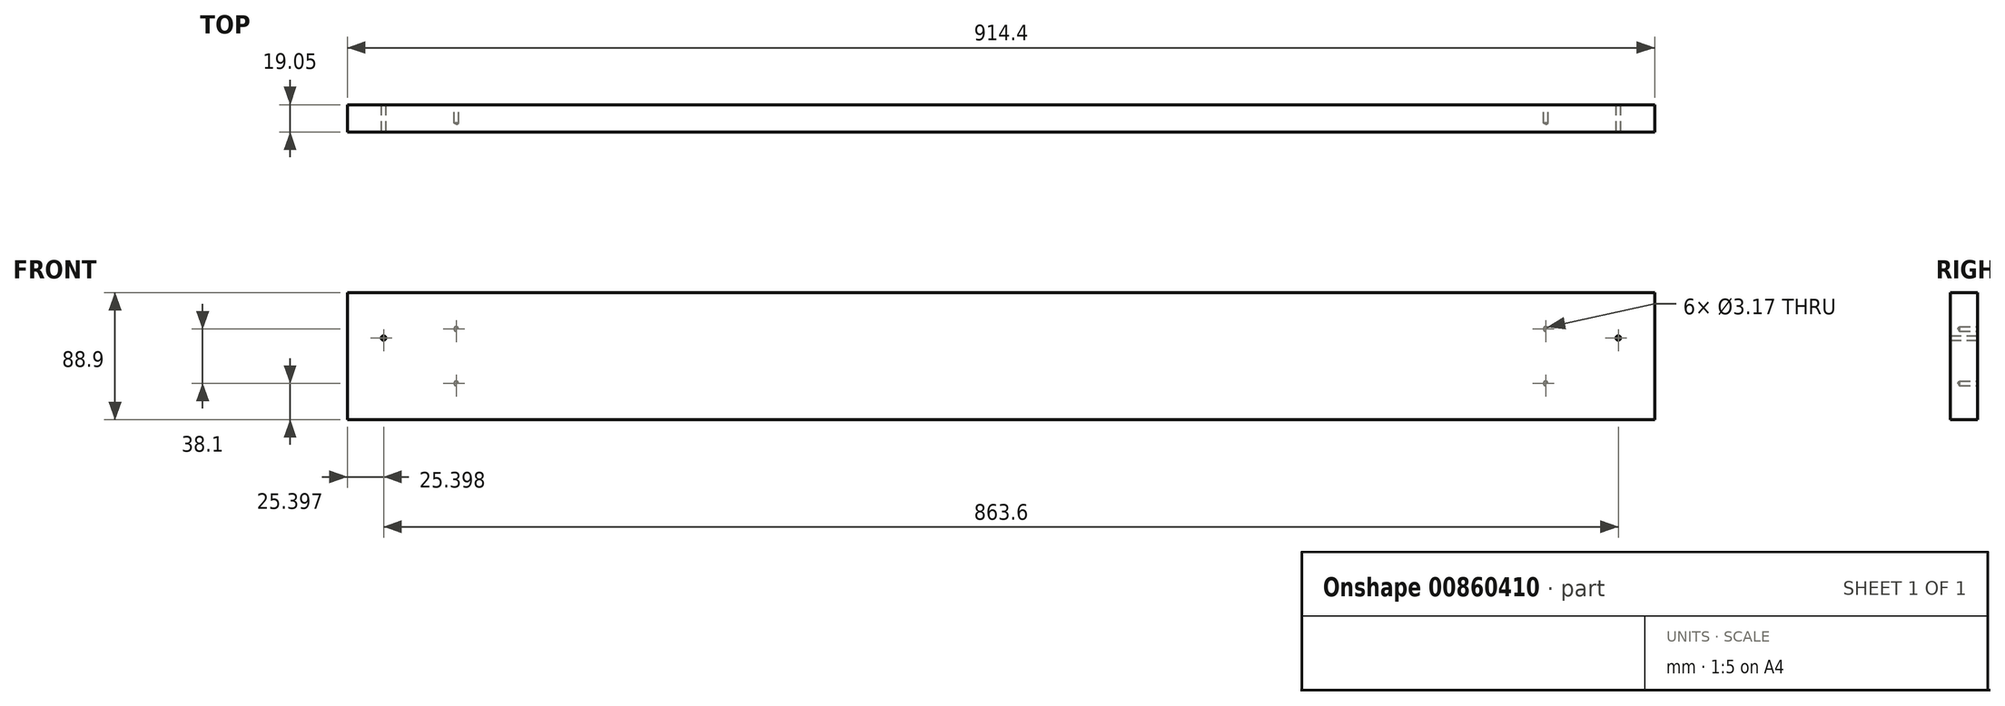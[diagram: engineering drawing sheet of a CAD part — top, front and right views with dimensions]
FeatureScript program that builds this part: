
annotation { "Feature Type Name" : "Feature", "Feature Type Description" : "" }
export const myFeature = defineFeature(function(context is Context, id is Id, definition is map)
    precondition{}
    {
        {
            var Q0;
            Q0=qCreatedBy(makeId("Front.planeOp"),FACE);
            var sketch = newSketch(context, id + "F0", { "sketchPlane" : qUnion([Q0])});
            skLineSegment(sketch, "E0.bottom", {"start": v(-572.65, 53.18) * mm, "end": v(341.75, 53.18) * mm});
            skLineSegment(sketch, "E0.top", {"start": v(-572.65, -35.72) * mm, "end": v(341.75, -35.72) * mm});
            skLineSegment(sketch, "E0.left", {"start": v(-572.65, 53.18) * mm, "end": v(-572.65, -35.72) * mm});
            skLineSegment(sketch, "E0.right", {"start": v(341.75, 53.18) * mm, "end": v(341.75, -35.72) * mm});
            skSolve(sketch);
        }
        {
            var Q0;
            Q0=makeQuery(id+"F0.imprint","IMPRINT",FACE,{"disambiguationData":[TD([[makeQuery(id+"F0.imprint","IMPRINT",EDGE,{"derivedFrom":sQuery(id+"F0.wireOp",EDGE,"E0.bottom")}),-1.0]])]});
            extrude(context, id + "F1", {"entities" : qUnion([Q0]), "depth" : 19.05 * mm, "offsetDistance" : 25.4 * mm});
        }
        {
            var Q0;
            Q0=makeQuery(id+"F1.opExtrude","CAP_FACE",FACE,{"disambiguationData":[OSD([sQuery(id+"F0.wireOp",EDGE,"E0.bottom"),sQuery(id+"F0.wireOp",EDGE,"E0.top"),sQuery(id+"F0.wireOp",EDGE,"E0.left"),sQuery(id+"F0.wireOp",EDGE,"E0.right")])],"isStart":true});
            var sketch = newSketch(context, id + "F2", { "sketchPlane" : qUnion([Q0])});
            skLineSegment(sketch, "E1", {"start": v(-265.55, -35.72) * mm, "end": v(-265.55, 53.18) * mm, "construction": true});
            skLineSegment(sketch, "E2", {"start": v(496.45, -35.72) * mm, "end": v(496.45, 53.18) * mm, "construction": true});
            skPoint(sketch, "E3", {"position": v(496.45, -10.32) * mm});
            skPoint(sketch, "E4", {"position": v(496.45, 27.78) * mm});
            skPoint(sketch, "E5", {"position": v(-265.55, -10.32) * mm});
            skPoint(sketch, "E6", {"position": v(-265.55, 27.78) * mm});
            skSolve(sketch);
        }
        {
            var Q0;
            Q0=sQuery(id+"F2.wireOp",VERTEX,"E5");
            var Q1;
            Q1=sQuery(id+"F2.wireOp",VERTEX,"E6");
            var Q2;
            Q2=sQuery(id+"F2.wireOp",VERTEX,"E3");
            var Q3;
            Q3=sQuery(id+"F2.wireOp",VERTEX,"E4");
            var Q4;
            Q4=makeQuery(id+"F1.opExtrude","SWEPT_BODY",BODY,{"disambiguationData":[OSD([sQuery(id+"F0.wireOp",EDGE,"E0.bottom"),sQuery(id+"F0.wireOp",EDGE,"E0.top"),sQuery(id+"F0.wireOp",EDGE,"E0.left"),sQuery(id+"F0.wireOp",EDGE,"E0.right")])]});
            hole(context, id + "F3", {"style" : HoleStyle.SIMPLE, "endStyle" : HoleEndStyle.BLIND, "holeDiameter" : 3.17 * mm, "majorDiameter" : 6.35 * mm, "holeDepth" : 12.7 * mm, "isTappedThrough" : true, "tappedDepth" : 12.7 * mm, "tapClearance" : 3, "locations" : qUnion([Q0, Q1, Q2, Q3]), "scope" : qUnion([Q4])});
        }
        {
            var Q0;
            Q0=makeQuery(id+"F1.opExtrude","CAP_FACE",FACE,{"disambiguationData":[OSD([sQuery(id+"F0.wireOp",EDGE,"E0.bottom"),sQuery(id+"F0.wireOp",EDGE,"E0.top"),sQuery(id+"F0.wireOp",EDGE,"E0.left"),sQuery(id+"F0.wireOp",EDGE,"E0.right")])],"isStart":true});
            var sketch = newSketch(context, id + "F4", { "sketchPlane" : qUnion([Q0])});
            skLineSegment(sketch, "E7", {"start": v(-316.35, -35.72) * mm, "end": v(-316.35, 53.18) * mm, "construction": true});
            skLineSegment(sketch, "E8", {"start": v(115.45, -35.72) * mm, "end": v(115.45, 53.18) * mm, "construction": true});
            skPoint(sketch, "E9", {"position": v(-316.35, 21.43) * mm});
            skPoint(sketch, "E10.MirrorP", {"position": v(547.25, 21.43) * mm});
            skLineSegment(sketch, "E11.MirrorCS", {"start": v(547.25, -35.72) * mm, "end": v(547.25, 53.18) * mm, "construction": true});
            skSolve(sketch);
        }
        {
            var Q0;
            Q0=sQuery(id+"F4.wireOp",VERTEX,"E9");
            var Q1;
            Q1=sQuery(id+"F4.wireOp",VERTEX,"E10.MirrorP");
            var Q2;
            Q2=makeQuery(id+"F1.opExtrude","SWEPT_BODY",BODY,{"disambiguationData":[OSD([sQuery(id+"F0.wireOp",EDGE,"E0.bottom"),sQuery(id+"F0.wireOp",EDGE,"E0.top"),sQuery(id+"F0.wireOp",EDGE,"E0.left"),sQuery(id+"F0.wireOp",EDGE,"E0.right")])]});
            hole(context, id + "F5", {"style" : HoleStyle.SIMPLE, "endStyle" : HoleEndStyle.THROUGH, "holeDiameter" : 3.17 * mm, "majorDiameter" : 6.35 * mm, "isTappedThrough" : true, "tappedDepth" : 12.7 * mm, "tapClearance" : 3, "locations" : qUnion([Q0, Q1]), "scope" : qUnion([Q2])});
        }
    });
